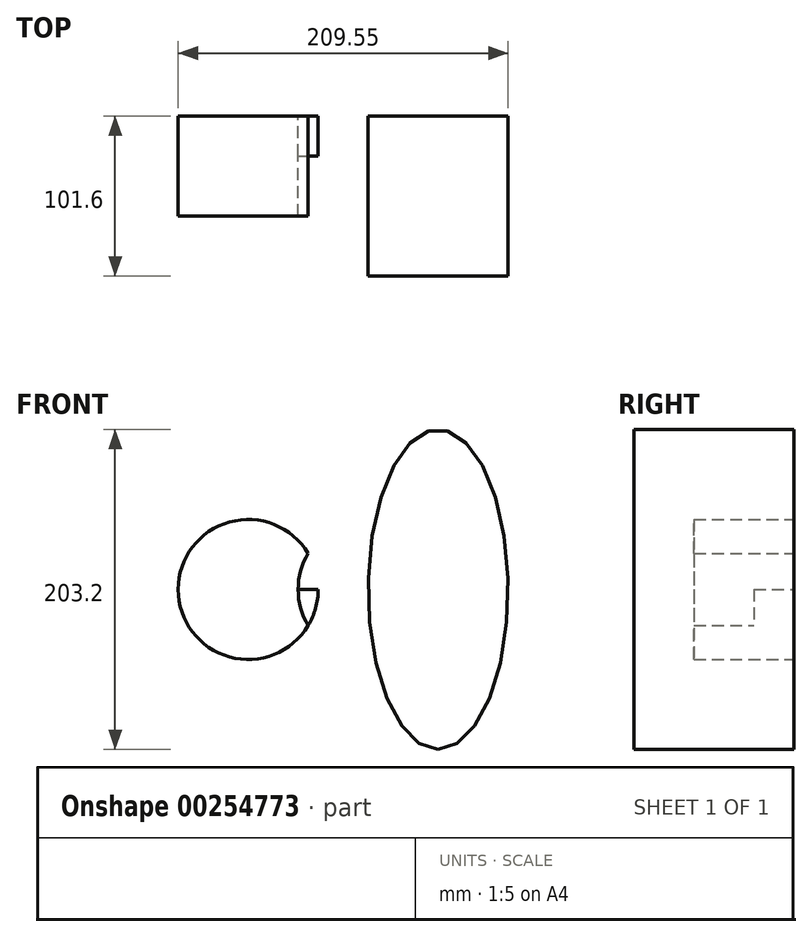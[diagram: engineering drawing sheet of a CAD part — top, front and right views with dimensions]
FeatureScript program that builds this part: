
annotation { "Feature Type Name" : "Feature", "Feature Type Description" : "" }
export const myFeature = defineFeature(function(context is Context, id is Id, definition is map)
    precondition{}
    {
        {
            var Q0;
            Q0=qCreatedBy(makeId("Front.planeOp"),FACE);
            var sketch = newSketch(context, id + "F0", { "sketchPlane" : qUnion([Q0])});
            skCircle(sketch, "E0", {"center": v(-76.2, 0) * mm, "radius": 44.45 * mm});
            skLineSegment(sketch, "E1", {"start": v(-76.2, 0) * mm, "end": v(-44.45, 0) * mm});
            skCircle(sketch, "E2", {"center": v(0, 0) * mm, "radius": 44.45 * mm});
            skLineSegment(sketch, "E3", {"start": v(-76.2, 0) * mm, "end": v(0, 0) * mm});
            skLineSegment(sketch, "E4", {"start": v(44.45, 0) * mm, "end": v(44.45, 101.6) * mm});
            skEllipse(sketch, "E5", {"center": v(44.45, 0) * mm, "majorRadius": 44.45 * mm, "minorRadius": 101.6 * mm, "majorAxis": v(-1, 0)});
            skSolve(sketch);
        }
        {
            var Q0;
            {var subQ0=sQuery(id+"F0.wireOp",EDGE,"E4");Q0=makeQuery(id+"F0.imprint","IMPRINT",FACE,{"disambiguationData":[TD([[makeQuery(id+"F0.imprint","IMPRINT",EDGE,{"derivedFrom":subQ0}),1.0]])]});}
            var Q1;
            {var subQ0=sQuery(id+"F0.wireOp",EDGE,"E4");Q1=makeQuery(id+"F0.imprint","IMPRINT",FACE,{"disambiguationData":[TD([[makeQuery(id+"F0.imprint","IMPRINT",EDGE,{"derivedFrom":subQ0}),-1.0]])]});}
            var Q2;
            {var subQ0=sQuery(id+"F0.wireOp",EDGE,"E2");var subQ1=makeQuery(id+"F0.imprint","INTERSECT",VERTEX,{"derivedFrom":[subQ0,sQuery(id+"F0.wireOp",EDGE,"E4")]});Q2=makeQuery(id+"F0.imprint","IMPRINT",FACE,{"disambiguationData":[TD([[makeQuery(id+"F0.imprint","IMPRINT",EDGE,{"disambiguationData":[TD([[subQ1,-1.0]])],"derivedFrom":subQ0}),1.0]])]});}
            extrude(context, id + "F1", {"entities" : qUnion([Q0, Q1, Q2]), "depth" : 101.6 * mm});
        }
        {
            var Q0;
            {var subQ0=sQuery(id+"F0.wireOp",EDGE,"E2");var subQ1=sQuery(id+"F0.wireOp",EDGE,"E0");var subQ2=makeQuery(id+"F0.imprint","INTERSECT",VERTEX,{"disambiguationData":[OD(0.0)],"derivedFrom":[subQ1,subQ0]});Q0=makeQuery(id+"F0.imprint","IMPRINT",FACE,{"disambiguationData":[TD([[makeQuery(id+"F0.imprint","IMPRINT",EDGE,{"disambiguationData":[TD([[subQ2,1.0]])],"derivedFrom":subQ1}),-1.0]])]});}
            var Q1;
            {var subQ0=sQuery(id+"F0.wireOp",EDGE,"E2");var subQ1=sQuery(id+"F0.wireOp",EDGE,"E0");var subQ2=makeQuery(id+"F0.imprint","INTERSECT",VERTEX,{"disambiguationData":[OD(0.0)],"derivedFrom":[subQ1,subQ0]});Q1=makeQuery(id+"F0.imprint","IMPRINT",FACE,{"disambiguationData":[TD([[makeQuery(id+"F0.imprint","IMPRINT",EDGE,{"disambiguationData":[TD([[subQ2,1.0]])],"derivedFrom":subQ1}),1.0]])]});}
            var Q2;
            {var subQ0=sQuery(id+"F0.wireOp",EDGE,"E2");var subQ1=sQuery(id+"F0.wireOp",EDGE,"E0");var subQ2=makeQuery(id+"F0.imprint","INTERSECT",VERTEX,{"disambiguationData":[OD(1.0)],"derivedFrom":[subQ1,subQ0]});Q2=makeQuery(id+"F0.imprint","IMPRINT",FACE,{"disambiguationData":[TD([[makeQuery(id+"F0.imprint","IMPRINT",EDGE,{"disambiguationData":[TD([[subQ2,-1.0]])],"derivedFrom":subQ1}),1.0]])]});}
            var Q3;
            {var subQ0=sQuery(id+"F0.wireOp",EDGE,"E2");var subQ1=sQuery(id+"F0.wireOp",EDGE,"E0");var subQ2=makeQuery(id+"F0.imprint","INTERSECT",VERTEX,{"disambiguationData":[OD(1.0)],"derivedFrom":[subQ1,subQ0]});Q3=makeQuery(id+"F0.imprint","IMPRINT",FACE,{"disambiguationData":[TD([[makeQuery(id+"F0.imprint","IMPRINT",EDGE,{"disambiguationData":[TD([[subQ2,-1.0]])],"derivedFrom":subQ1}),-1.0]])]});}
            extrude(context, id + "F2", {"entities" : qUnion([Q0, Q1, Q2, Q3]), "operationType" : NewBodyOperationType.ADD, "depth" : 63.5 * mm});
        }
        {
            var Q0;
            {var subQ0=sQuery(id+"F0.wireOp",EDGE,"E2");var subQ1=sQuery(id+"F0.wireOp",EDGE,"E0");var subQ2=makeQuery(id+"F0.imprint","INTERSECT",VERTEX,{"disambiguationData":[OD(0.0)],"derivedFrom":[subQ1,subQ0]});Q0=makeQuery(id+"F0.imprint","IMPRINT",FACE,{"disambiguationData":[TD([[makeQuery(id+"F0.imprint","IMPRINT",EDGE,{"disambiguationData":[TD([[subQ2,-1.0]])],"derivedFrom":subQ1}),1.0]])]});}
            extrude(context, id + "F3", {"entities" : qUnion([Q0]), "operationType" : NewBodyOperationType.ADD, "depth" : 25.4 * mm});
        }
    });
